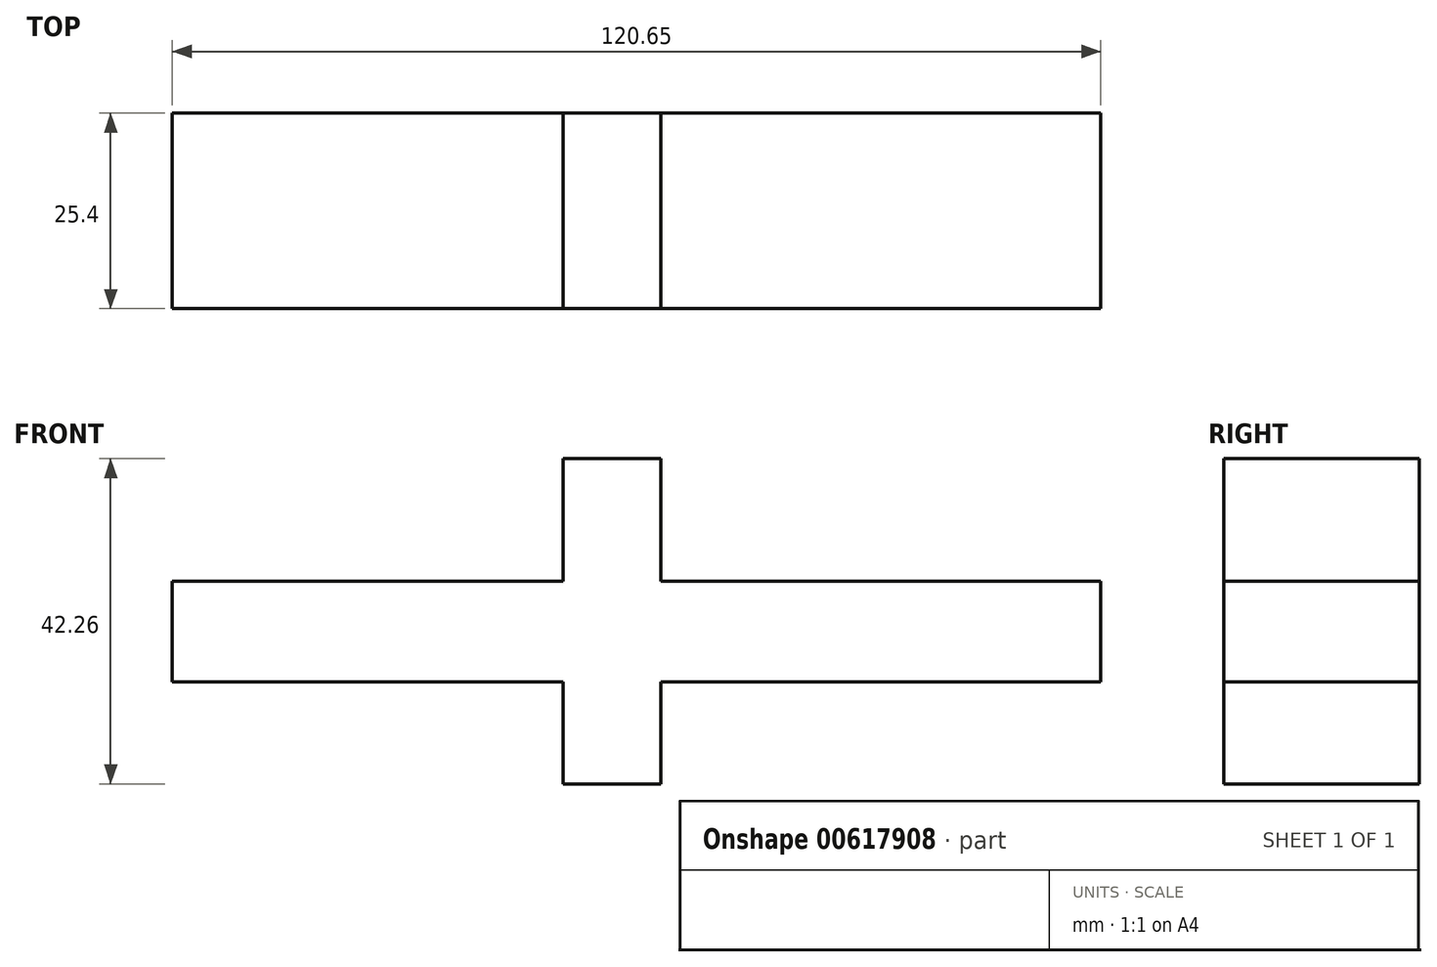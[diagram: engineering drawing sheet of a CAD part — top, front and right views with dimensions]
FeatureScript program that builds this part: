
annotation { "Feature Type Name" : "Feature", "Feature Type Description" : "" }
export const myFeature = defineFeature(function(context is Context, id is Id, definition is map)
    precondition{}
    {
        {
            var Q0;
            Q0=qCreatedBy(makeId("Front.planeOp"),FACE);
            var sketch = newSketch(context, id + "F0", { "sketchPlane" : qUnion([Q0])});
            skLineSegment(sketch, "E0", {"start": v(0, 0) * mm, "end": v(0, 15.9) * mm});
            skLineSegment(sketch, "E1", {"start": v(0, 15.9) * mm, "end": v(12.7, 15.9) * mm});
            skLineSegment(sketch, "E2", {"start": v(12.7, 15.9) * mm, "end": v(12.7, 0) * mm});
            skLineSegment(sketch, "E3", {"start": v(12.7, 0) * mm, "end": v(69.85, 0) * mm});
            skLineSegment(sketch, "E4", {"start": v(69.85, 0) * mm, "end": v(69.85, -13.13) * mm});
            skLineSegment(sketch, "E5", {"start": v(69.85, -13.13) * mm, "end": v(12.7, -13.13) * mm});
            skLineSegment(sketch, "E6", {"start": v(12.7, -13.13) * mm, "end": v(12.7, -26.36) * mm});
            skLineSegment(sketch, "E7", {"start": v(12.7, -26.36) * mm, "end": v(0, -26.36) * mm});
            skLineSegment(sketch, "E8", {"start": v(0, -26.36) * mm, "end": v(0, -13.13) * mm});
            skLineSegment(sketch, "E9", {"start": v(0, -13.13) * mm, "end": v(-50.8, -13.13) * mm});
            skLineSegment(sketch, "E10", {"start": v(-50.8, -13.13) * mm, "end": v(-50.8, 0) * mm});
            skLineSegment(sketch, "E11", {"start": v(-50.8, 0) * mm, "end": v(0, 0) * mm});
            skSolve(sketch);
        }
        {
            var Q0;
            Q0=makeQuery(id+"F0.imprint","IMPRINT",FACE,{"disambiguationData":[TD([[makeQuery(id+"F0.imprint","IMPRINT",EDGE,{"derivedFrom":sQuery(id+"F0.wireOp",EDGE,"E0")}),-1.0]])]});
            extrude(context, id + "F1", {"entities" : qUnion([Q0]), "depth" : 25.4 * mm, "offsetDistance" : 25.4 * mm});
        }
    });
